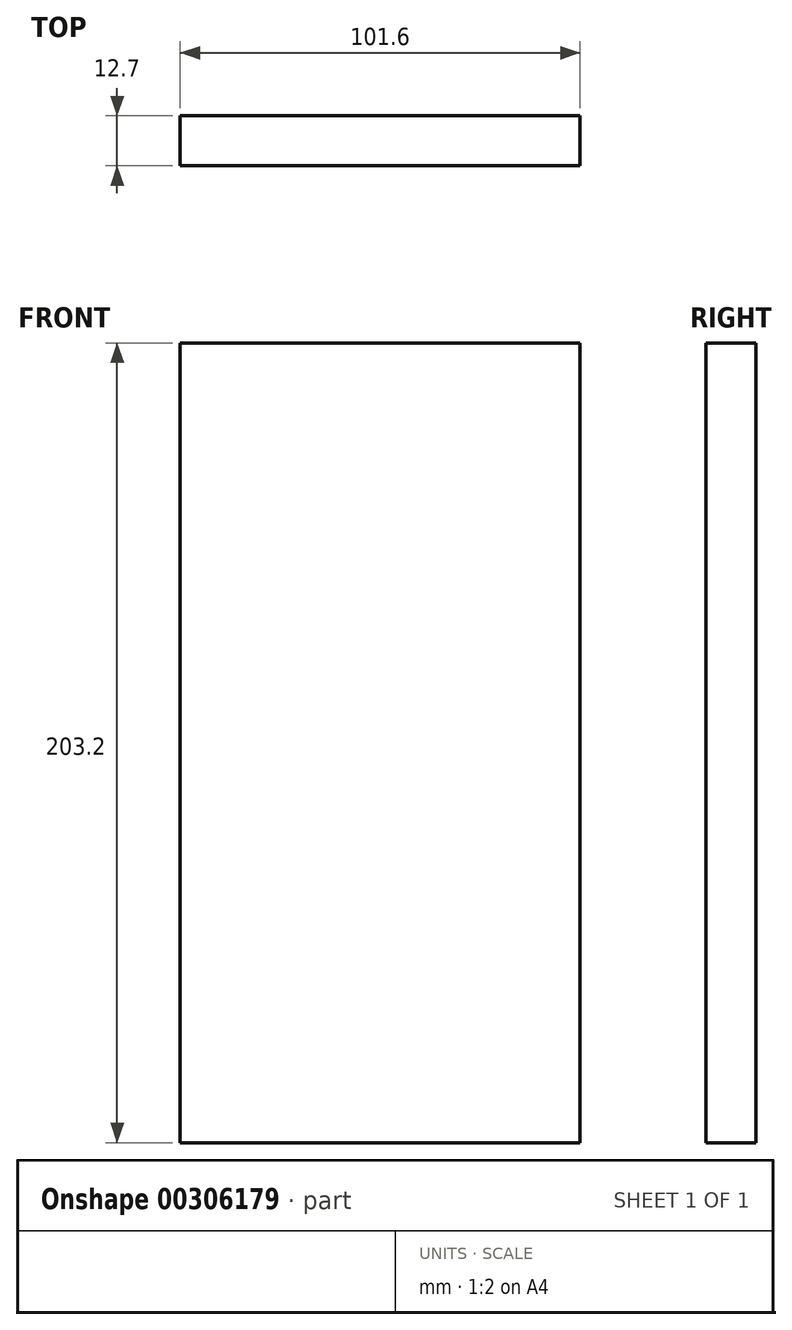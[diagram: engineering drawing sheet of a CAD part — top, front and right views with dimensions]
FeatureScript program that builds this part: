
annotation { "Feature Type Name" : "Feature", "Feature Type Description" : "" }
export const myFeature = defineFeature(function(context is Context, id is Id, definition is map)
    precondition{}
    {
        {
            var Q0;
            Q0=qCreatedBy(makeId("Front.planeOp"),FACE);
            var sketch = newSketch(context, id + "F0", { "sketchPlane" : qUnion([Q0])});
            skLineSegment(sketch, "E0.bottom", {"start": v(-21.94, 156.58) * mm, "end": v(79.66, 156.58) * mm});
            skLineSegment(sketch, "E0.top", {"start": v(-21.94, -46.62) * mm, "end": v(79.66, -46.62) * mm});
            skLineSegment(sketch, "E0.left", {"start": v(-21.94, 156.58) * mm, "end": v(-21.94, -46.62) * mm});
            skLineSegment(sketch, "E0.right", {"start": v(79.66, 156.58) * mm, "end": v(79.66, -46.62) * mm});
            skSolve(sketch);
        }
        {
            var Q0;
            Q0 = qSketchRegion(id + "F0", true);
            extrude(context, id + "F1", {"entities" : qUnion([Q0]), "depth" : 12.7 * mm});
        }
    });
